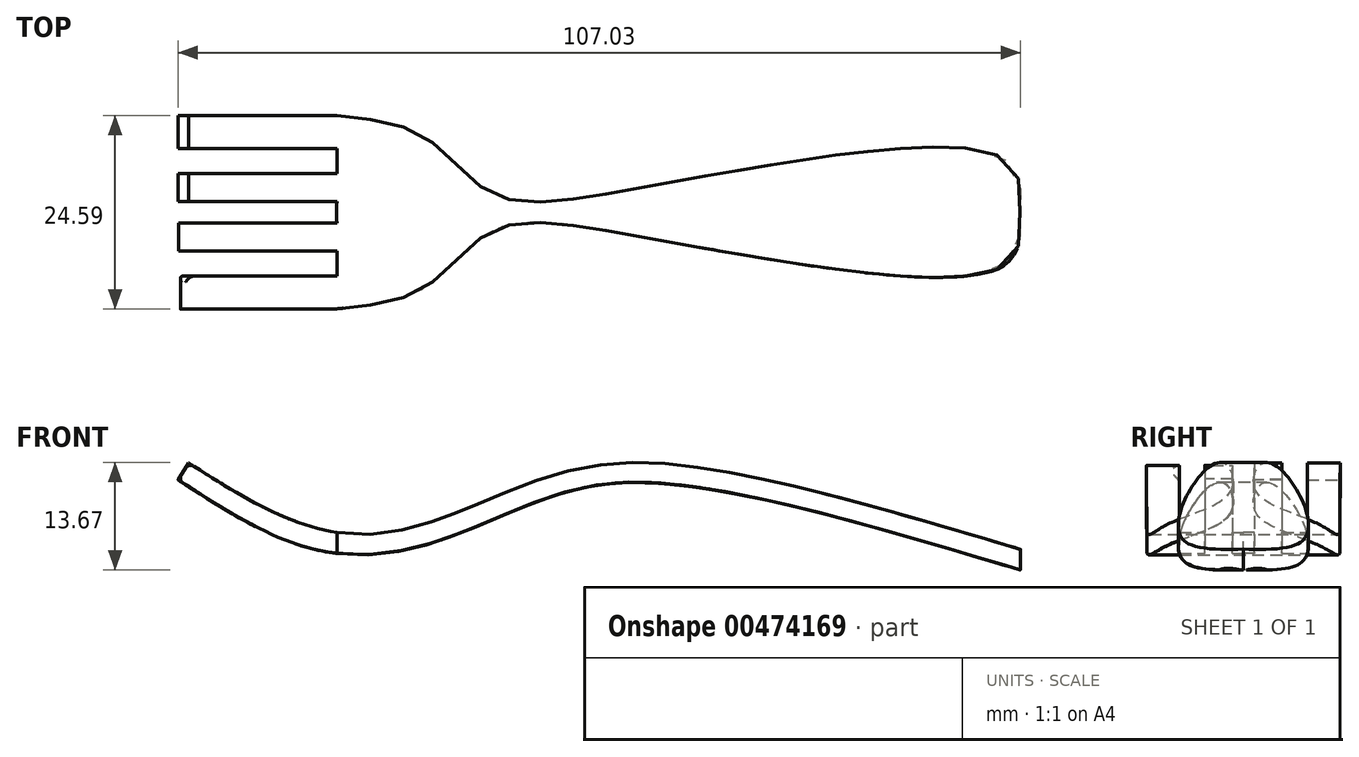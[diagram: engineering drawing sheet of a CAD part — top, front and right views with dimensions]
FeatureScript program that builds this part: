
annotation { "Feature Type Name" : "Feature", "Feature Type Description" : "" }
export const myFeature = defineFeature(function(context is Context, id is Id, definition is map)
    precondition{}
    {
        {
            var Q0;
            Q0=qCreatedBy(makeId("Front.planeOp"),FACE);
            var sketch = newSketch(context, id + "F0", { "sketchPlane" : qUnion([Q0])});
            skFitSpline(sketch, "E0", {"points": [v(0, 0) * mm, v(12.63, -7.05) * mm, v(25.55, -8.81) * mm, v(42.3, -2.94) * mm, v(59.33, 0) * mm, v(106.32, -11.16) * mm], "startDerivative": vector(74.66, -47.6) * mm, "endDerivative": vector(173.6, -51.56) * mm});
            skFitSpline(sketch, "E1.0", {"points": [v(-1.37, -2.14) * mm, v(0.19, -3.13) * mm, v(3.33, -5.14) * mm, v(8.2, -7.92) * mm, v(13.3, -10.18) * mm, v(17.83, -11.34) * mm, v(21.65, -11.66) * mm, v(24.11, -11.57) * mm, v(26.13, -11.3) * mm, v(28.16, -10.91) * mm, v(30.67, -10.23) * mm, v(33.66, -9.19) * mm, v(36.6, -8.02) * mm, v(39.49, -6.82) * mm, v(41.8, -5.86) * mm, v(43.57, -5.16) * mm, v(45.3, -4.51) * mm, v(47.4, -3.81) * mm, v(49.92, -3.16) * mm, v(52.51, -2.7) * mm, v(55.3, -2.46) * mm, v(57.88, -2.46) * mm, v(60.13, -2.59) * mm, v(62.54, -2.81) * mm, v(65.78, -3.26) * mm, v(70.02, -4.02) * mm, v(76.07, -5.33) * mm, v(84.26, -7.4) * mm, v(94.75, -10.38) * mm, v(101.98, -12.52) * mm, v(105.6, -13.6) * mm]});
            skLineSegment(sketch, "E2", {"start": v(-1.37, -2.14) * mm, "end": v(0, 0) * mm});
            skLineSegment(sketch, "E3", {"start": v(105.6, -13.6) * mm, "end": v(106.32, -11.16) * mm});
            skSolve(sketch);
        }
        {
            var Q0;
            Q0=makeQuery(id+"F0.imprint","IMPRINT",FACE,{"disambiguationData":[TD([[makeQuery(id+"F0.imprint","IMPRINT",EDGE,{"derivedFrom":sQuery(id+"F0.wireOp",EDGE,"E0")}),-1.0]])]});
            extrude(context, id + "F1", {"entities" : qUnion([Q0]), "depth" : 25.4 * mm});
        }
        {
            var Q0;
            Q0=qCreatedBy(makeId("Top.planeOp"),FACE);
            var sketch = newSketch(context, id + "F2", { "sketchPlane" : qUnion([Q0])});
            skPoint(sketch, "E4.0", {"position": v(106.32, -12.7) * mm});
            skPoint(sketch, "E5.0", {"position": v(-1.37, -12.7) * mm});
            skLineSegment(sketch, "E6", {"start": v(-1.37, -21.43) * mm, "end": v(-1.37, -23.26) * mm});
            skLineSegment(sketch, "E7", {"start": v(-1.37, -23.26) * mm, "end": v(-1.37, -25.3) * mm});
            skPoint(sketch, "E7.endSnap0", {"position": v(-1.37, -14.07) * mm});
            skLineSegment(sketch, "E8", {"start": v(-1.37, -25.3) * mm, "end": v(18.8, -25.27) * mm});
            skLineSegment(sketch, "E9", {"start": v(105.56, -13) * mm, "end": v(18.77, -13) * mm, "construction": true});
            skFitSpline(sketch, "E10.MirrorCS", {"points": [v(18.8, -0.74) * mm, v(29.95, -3.45) * mm, v(37.98, -10.35) * mm, v(54.92, -10.35) * mm, v(102.94, -5.9) * mm, v(105.65, -10.79) * mm, v(105.56, -13) * mm], "startDerivative": vector(77.08, -7.13) * mm, "endDerivative": vector(-2.35, -30.51) * mm});
            skLineSegment(sketch, "E11.MirrorCS", {"start": v(-1.37, -0.71) * mm, "end": v(18.8, -0.74) * mm});
            skLineSegment(sketch, "E12.MirrorCS", {"start": v(-1.37, -11.63) * mm, "end": v(18.8, -11.63) * mm});
            skLineSegment(sketch, "E13.bottom", {"start": v(-4.94, 3.6) * mm, "end": v(114.74, 3.6) * mm});
            skLineSegment(sketch, "E13.top", {"start": v(-4.94, -32.67) * mm, "end": v(114.74, -32.67) * mm});
            skLineSegment(sketch, "E13.left", {"start": v(-4.94, 3.6) * mm, "end": v(-4.94, -32.67) * mm});
            skLineSegment(sketch, "E13.right", {"start": v(114.74, 3.6) * mm, "end": v(114.74, -32.67) * mm});
            skLineSegment(sketch, "E14", {"start": v(-1.37, -0.71) * mm, "end": v(-1.37, -4.9) * mm});
            skLineSegment(sketch, "E15", {"start": v(-1.37, -4.9) * mm, "end": v(18.8, -4.9) * mm});
            skLineSegment(sketch, "E16", {"start": v(18.8, -4.9) * mm, "end": v(18.8, -8.11) * mm});
            skLineSegment(sketch, "E17", {"start": v(18.8, -8.11) * mm, "end": v(-1.34, -8.11) * mm});
            skLineSegment(sketch, "E18", {"start": v(-1.34, -8.11) * mm, "end": v(-1.37, -11.63) * mm});
            skLineSegment(sketch, "E19", {"start": v(18.8, -11.63) * mm, "end": v(18.77, -13) * mm});
            skLineSegment(sketch, "E20.MirrorCS", {"start": v(18.8, -17.9) * mm, "end": v(-1.34, -17.9) * mm});
            skLineSegment(sketch, "E21.MirrorCS", {"start": v(-1.37, -21.12) * mm, "end": v(18.8, -21.12) * mm});
            skLineSegment(sketch, "E22.MirrorCS", {"start": v(-1.37, -14.38) * mm, "end": v(18.8, -14.38) * mm});
            skLineSegment(sketch, "E23.MirrorCS", {"start": v(18.8, -14.38) * mm, "end": v(18.77, -13) * mm});
            skFitSpline(sketch, "E24.MirrorCS", {"points": [v(18.8, -25.27) * mm, v(29.95, -22.57) * mm, v(37.98, -15.67) * mm, v(54.92, -15.67) * mm, v(102.94, -20.12) * mm, v(105.65, -15.23) * mm, v(105.56, -13) * mm], "startDerivative": vector(77.08, 7.13) * mm, "endDerivative": vector(-2.35, 30.51) * mm});
            skLineSegment(sketch, "E25.MirrorCS", {"start": v(18.8, -21.12) * mm, "end": v(18.8, -17.9) * mm});
            skLineSegment(sketch, "E26.MirrorCS", {"start": v(-1.37, -25.3) * mm, "end": v(-1.37, -21.12) * mm});
            skLineSegment(sketch, "E27.MirrorCS", {"start": v(-1.34, -17.9) * mm, "end": v(-1.37, -14.38) * mm});
            skSolve(sketch);
        }
        {
            var Q0;
            Q0=makeQuery(id+"F2.imprint","IMPRINT",FACE,{"disambiguationData":[TD([[makeQuery(id+"F2.imprint","IMPRINT",EDGE,{"derivedFrom":sQuery(id+"F2.wireOp",EDGE,"E10.MirrorCS")}),1.0]])]});
            extrude(context, id + "F3", {"entities" : qUnion([Q0]), "operationType" : NewBodyOperationType.REMOVE, "endBound" : BoundingType.SYMMETRIC, "oppositeDirection" : true, "depth" : 50.8 * mm});
        }
        {
            var Q0;
            Q0=makeQuery(id+"F3.boolean.opBoolean","INTERSECT",EDGE,{"disambiguationData":[OD(1.0)],"derivedFrom":[makeQuery(id+"F1.opExtrude","SWEPT_FACE",FACE,{"disambiguationData":[OSD([sQuery(id+"F0.wireOp",EDGE,"E1.0")])]}),makeQuery(id+"F3.opExtrude","SWEPT_FACE",FACE,{"disambiguationData":[OSD([sQuery(id+"F2.wireOp",EDGE,"E24.MirrorCS")])]})]});
            fillet(context, id + "F4", {"entities" : qUnion([Q0]), "radius" : 0.03 * mm, "tangentPropagation" : true, "allowEdgeOverflow" : false});
        }
        {
            var Q0;
            {var subQ0=sQuery(id+"F0.wireOp",EDGE,"E0");var subQ1=sQuery(id+"F0.wireOp",EDGE,"E2");Q0=makeQuery(id+"F3.boolean.opBoolean","SPLIT",EDGE,{"disambiguationData":[TD([makeQuery(id+"F3.opExtrude","SWEPT_FACE",FACE,{"disambiguationData":[OSD([sQuery(id+"F2.wireOp",EDGE,"E21.MirrorCS")])]})])],"derivedFrom":makeQuery(id+"F1.opExtrude","SWEPT_EDGE",EDGE,{"disambiguationData":[OSD([subQ0,subQ1])]})});}
            var Q1;
            Q1=makeQuery(id+"F3.boolean.opBoolean","INTERSECT",EDGE,{"derivedFrom":[makeQuery(id+"F1.opExtrude","SWEPT_FACE",FACE,{"disambiguationData":[OSD([sQuery(id+"F0.wireOp",EDGE,"E2")])]}),makeQuery(id+"F3.opExtrude","SWEPT_FACE",FACE,{"disambiguationData":[OSD([sQuery(id+"F2.wireOp",EDGE,"E8")])]})]});
            var Q2;
            Q2=makeQuery(id+"F3.boolean.opBoolean","INTERSECT",EDGE,{"derivedFrom":[makeQuery(id+"F1.opExtrude","SWEPT_FACE",FACE,{"disambiguationData":[OSD([sQuery(id+"F0.wireOp",EDGE,"E2")])]}),makeQuery(id+"F3.opExtrude","SWEPT_FACE",FACE,{"disambiguationData":[OSD([sQuery(id+"F2.wireOp",EDGE,"E21.MirrorCS")])]})]});
            var Q3;
            {var subQ0=sQuery(id+"F0.wireOp",EDGE,"E1.0");var subQ1=sQuery(id+"F0.wireOp",EDGE,"E2");Q3=makeQuery(id+"F3.boolean.opBoolean","SPLIT",EDGE,{"disambiguationData":[TD([makeQuery(id+"F3.opExtrude","SWEPT_FACE",FACE,{"disambiguationData":[OSD([sQuery(id+"F2.wireOp",EDGE,"E21.MirrorCS")])]})])],"derivedFrom":makeQuery(id+"F1.opExtrude","SWEPT_EDGE",EDGE,{"disambiguationData":[OSD([subQ0,subQ1])]})});}
            var Q4;
            {var subQ0=sQuery(id+"F0.wireOp",EDGE,"E0");var subQ1=sQuery(id+"F0.wireOp",EDGE,"E2");Q4=makeQuery(id+"F3.boolean.opBoolean","SPLIT",EDGE,{"disambiguationData":[TD([makeQuery(id+"F3.opExtrude","SWEPT_FACE",FACE,{"disambiguationData":[OSD([sQuery(id+"F2.wireOp",EDGE,"E22.MirrorCS")])]})])],"derivedFrom":makeQuery(id+"F1.opExtrude","SWEPT_EDGE",EDGE,{"disambiguationData":[OSD([subQ0,subQ1])]})});}
            var Q5;
            Q5=makeQuery(id+"F3.boolean.opBoolean","INTERSECT",EDGE,{"derivedFrom":[makeQuery(id+"F1.opExtrude","SWEPT_FACE",FACE,{"disambiguationData":[OSD([sQuery(id+"F0.wireOp",EDGE,"E1.0")])]}),makeQuery(id+"F3.opExtrude","SWEPT_FACE",FACE,{"disambiguationData":[OSD([sQuery(id+"F2.wireOp",EDGE,"E27.MirrorCS")])]})]});
            fillet(context, id + "F5", {"entities" : qUnion([Q0, Q1, Q2, Q3, Q4, Q5]), "radius" : 0.76 * mm, "tangentPropagation" : true, "allowEdgeOverflow" : false});
        }
    });
